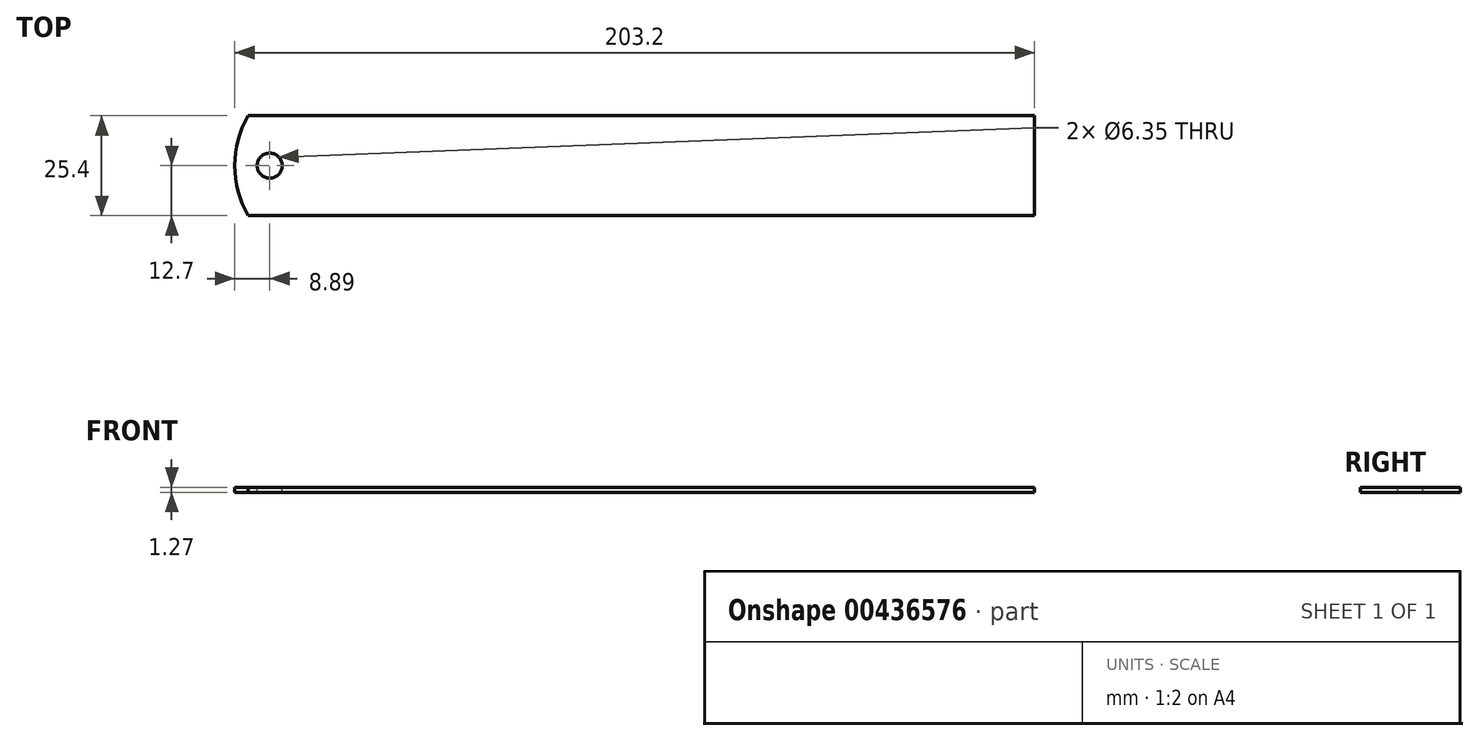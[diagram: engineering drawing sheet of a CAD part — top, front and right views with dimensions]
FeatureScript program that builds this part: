
annotation { "Feature Type Name" : "Feature", "Feature Type Description" : "" }
export const myFeature = defineFeature(function(context is Context, id is Id, definition is map)
    precondition{}
    {
        {
            var Q0;
            Q0=qCreatedBy(makeId("Front.planeOp"),FACE);
            var sketch = newSketch(context, id + "F0", { "sketchPlane" : qUnion([Q0])});
            skLineSegment(sketch, "E0.bottom", {"start": v(-203.2, 1.27) * mm, "end": v(0, 1.27) * mm});
            skLineSegment(sketch, "E0.top", {"start": v(-203.2, 0) * mm, "end": v(0, 0) * mm});
            skLineSegment(sketch, "E0.left", {"start": v(-203.2, 1.27) * mm, "end": v(-203.2, 0) * mm});
            skLineSegment(sketch, "E0.right", {"start": v(0, 1.27) * mm, "end": v(0, 0) * mm});
            skSolve(sketch);
        }
        {
            var Q0;
            Q0 = qSketchRegion(id + "F0", true);
            extrude(context, id + "F1", {"entities" : qUnion([Q0]), "depth" : 25.4 * mm});
        }
        {
            var Q0;
            Q0=makeQuery(id+"F1.opExtrude","SWEPT_FACE",FACE,{"disambiguationData":[OSD([sQuery(id+"F0.wireOp",EDGE,"E0.bottom")])]});
            var sketch = newSketch(context, id + "F2", { "sketchPlane" : qUnion([Q0])});
            skArc(sketch, "E1", {"start": v(-199.8, 0) * mm, "mid": v(-203.2, -12.7) * mm, "end": v(-199.8, -25.4) * mm});
            skPoint(sketch, "E2", {"position": v(-203.2, -12.7) * mm});
            skLineSegment(sketch, "E3", {"start": v(-199.8, 0) * mm, "end": v(-203.2, 0) * mm});
            skLineSegment(sketch, "E4", {"start": v(-203.2, 0) * mm, "end": v(-203.2, -25.4) * mm});
            skLineSegment(sketch, "E5", {"start": v(-203.2, -25.4) * mm, "end": v(-199.8, -25.4) * mm});
            skCircle(sketch, "E6", {"center": v(-194.3, -12.7) * mm, "radius": 3.18 * mm});
            skSolve(sketch);
        }
        {
            var Q0;
            Q0 = qSketchRegion(id + "F2", true);
            extrude(context, id + "F3", {"entities" : qUnion([Q0]), "operationType" : NewBodyOperationType.REMOVE, "oppositeDirection" : true, "depth" : 25.4 * mm});
        }
    });
